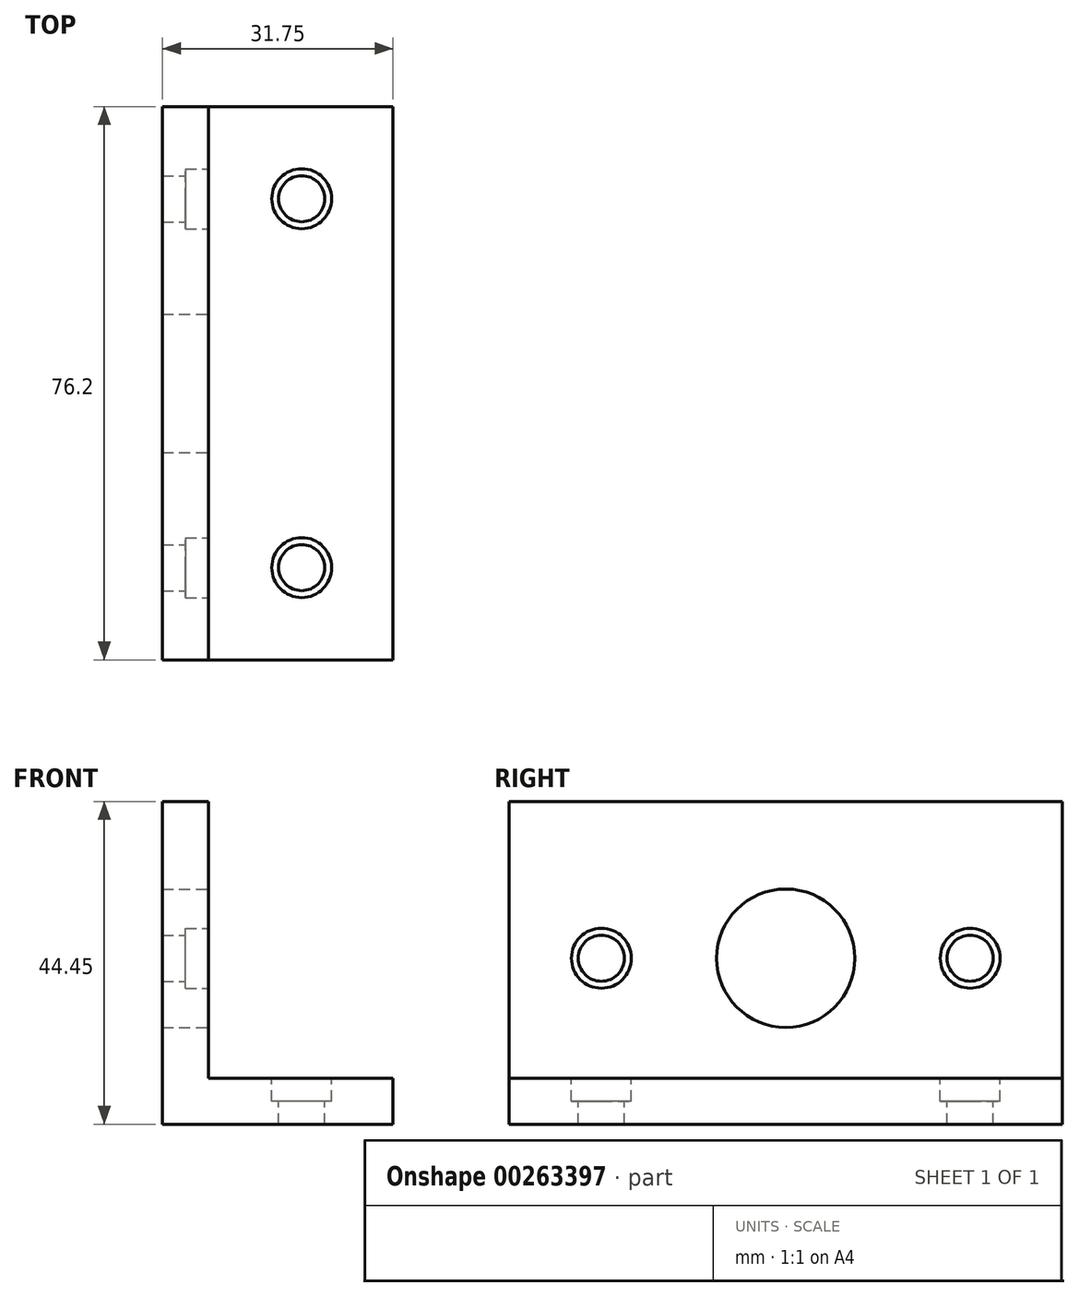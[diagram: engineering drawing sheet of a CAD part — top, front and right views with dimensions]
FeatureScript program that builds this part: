
annotation { "Feature Type Name" : "Feature", "Feature Type Description" : "" }
export const myFeature = defineFeature(function(context is Context, id is Id, definition is map)
    precondition{}
    {
        {
            var Q0;
            Q0=qCreatedBy(makeId("Front.planeOp"),FACE);
            var sketch = newSketch(context, id + "F0", { "sketchPlane" : qUnion([Q0])});
            skLineSegment(sketch, "E0", {"start": v(0, 0) * mm, "end": v(0, 44.45) * mm});
            skLineSegment(sketch, "E1", {"start": v(0, 44.45) * mm, "end": v(6.35, 44.45) * mm});
            skLineSegment(sketch, "E2", {"start": v(6.35, 44.45) * mm, "end": v(6.35, 6.35) * mm});
            skLineSegment(sketch, "E3", {"start": v(6.35, 6.35) * mm, "end": v(31.75, 6.35) * mm});
            skLineSegment(sketch, "E4", {"start": v(31.75, 6.35) * mm, "end": v(31.75, 0) * mm});
            skLineSegment(sketch, "E5", {"start": v(31.75, 0) * mm, "end": v(0, 0) * mm});
            skSolve(sketch);
        }
        {
            var Q0;
            Q0 = qSketchRegion(id + "F0", true);
            extrude(context, id + "F1", {"entities" : qUnion([Q0]), "depth" : 76.2 * mm, "offsetDistance" : 25.4 * mm});
        }
        {
            var Q0;
            Q0=makeQuery(id+"F1.opExtrude","SWEPT_FACE",FACE,{"disambiguationData":[OSD([sQuery(id+"F0.wireOp",EDGE,"E2")])]});
            var sketch = newSketch(context, id + "F2", { "sketchPlane" : qUnion([Q0])});
            skPoint(sketch, "E6", {"position": v(-38.1, 22.86) * mm});
            skPoint(sketch, "E6.positionSnap0", {"position": v(-38.1, 6.35) * mm});
            skPoint(sketch, "E6.positionSnap1", {"position": v(-76.2, 22.86) * mm});
            skSolve(sketch);
        }
        {
            var Q0;
            {var subQ0=sQuery(id+"F0.wireOp",EDGE,"E2");Q0=makeQuery(id+"F2.imprint","IMPRINT",FACE,{"disambiguationData":[TD([[makeQuery(id+"F2.imprint","IMPRINT",EDGE,{"derivedFrom":makeQuery(id+"F1.opExtrude","CAP_EDGE",EDGE,{"disambiguationData":[OSD([subQ0])],"isStart":true})}),-1.0]])]});}
            var sketch = newSketch(context, id + "F3", { "sketchPlane" : qUnion([Q0])});
            skPoint(sketch, "E7", {"position": v(-63.5, 22.86) * mm});
            skPoint(sketch, "E8", {"position": v(-12.7, 22.86) * mm});
            skSolve(sketch);
        }
        {
            var Q0;
            Q0=makeQuery(id+"F1.opExtrude","SWEPT_FACE",FACE,{"disambiguationData":[OSD([sQuery(id+"F0.wireOp",EDGE,"E3")])]});
            var sketch = newSketch(context, id + "F4", { "sketchPlane" : qUnion([Q0])});
            skPoint(sketch, "E9", {"position": v(19.05, -76.2) * mm});
            skPoint(sketch, "E10", {"position": v(19.17, -63.5) * mm});
            skPoint(sketch, "E11", {"position": v(19.17, -12.7) * mm});
            skSolve(sketch);
        }
        {
            var Q0;
            Q0=sQuery(id+"F3.wireOp",VERTEX,"E7");
            var Q1;
            Q1=sQuery(id+"F3.wireOp",VERTEX,"E8");
            var Q2;
            Q2=sQuery(id+"F4.wireOp",VERTEX,"E11");
            var Q3;
            Q3=sQuery(id+"F4.wireOp",VERTEX,"E10");
            var Q4;
            Q4=makeQuery(id+"F1.opExtrude","SWEPT_BODY",BODY,{"disambiguationData":[OSD([sQuery(id+"F0.wireOp",EDGE,"E0"),sQuery(id+"F0.wireOp",EDGE,"E1"),sQuery(id+"F0.wireOp",EDGE,"E2"),sQuery(id+"F0.wireOp",EDGE,"E3"),sQuery(id+"F0.wireOp",EDGE,"E4"),sQuery(id+"F0.wireOp",EDGE,"E5")])]});
            hole(context, id + "F5", {"style" : HoleStyle.C_BORE, "endStyle" : HoleEndStyle.THROUGH, "holeDiameter" : 6.35 * mm, "cBoreDiameter" : 8.25 * mm, "cBoreDepth" : 3.17 * mm, "majorDiameter" : 6.35 * mm, "isTappedThrough" : true, "tappedDepth" : 12.7 * mm, "tapClearance" : 3, "startFromSketch" : true, "locations" : qUnion([Q0, Q1, Q2, Q3]), "scope" : qUnion([Q4])});
        }
        {
            var Q0;
            Q0=sQuery(id+"F2.wireOp",VERTEX,"E6");
            var Q1;
            Q1=makeQuery(id+"F1.opExtrude","SWEPT_BODY",BODY,{"disambiguationData":[OSD([sQuery(id+"F0.wireOp",EDGE,"E0"),sQuery(id+"F0.wireOp",EDGE,"E1"),sQuery(id+"F0.wireOp",EDGE,"E2"),sQuery(id+"F0.wireOp",EDGE,"E3"),sQuery(id+"F0.wireOp",EDGE,"E4"),sQuery(id+"F0.wireOp",EDGE,"E5")])]});
            hole(context, id + "F6", {"style" : HoleStyle.SIMPLE, "endStyle" : HoleEndStyle.THROUGH, "holeDiameter" : 19.05 * mm, "majorDiameter" : 6.35 * mm, "isTappedThrough" : true, "tappedDepth" : 12.7 * mm, "tapClearance" : 3, "startFromSketch" : true, "locations" : qUnion([Q0]), "scope" : qUnion([Q1])});
        }
    });
